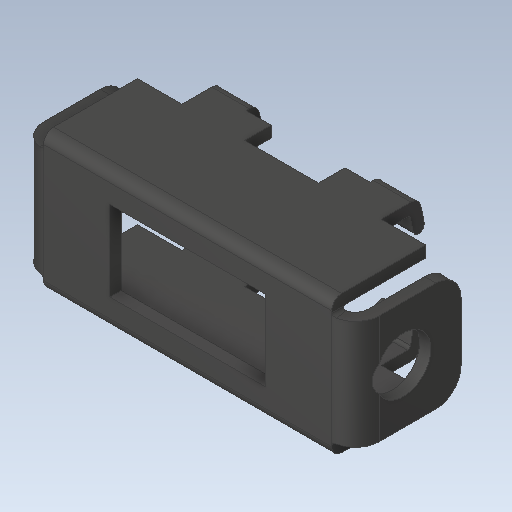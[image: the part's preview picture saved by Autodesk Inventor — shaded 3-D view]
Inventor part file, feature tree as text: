
AUTODESK INVENTOR PART (.ipt)
format: ipt  version: 2020.1 (Build 241239000, 239)  size: 245,248 bytes
history: native  units: mm
features: other x3, sketch x2
ambient origin geometry x8: Origin, YZ Plane, XZ Plane, XY Plane, X Axis, Y Axis, Z Axis, Center Point
bodies: Solid1 (feature_tree)
feature tree (5):
  other  "Bend Part1"
  other  "Bend Part2"
  sketch  "Sketch1"  dims[d0=0.5mm d1=90.0deg]
  sketch  "Sketch3"  dims[d2=0.5mm d3=90.0deg]
  other  "PartBody"
